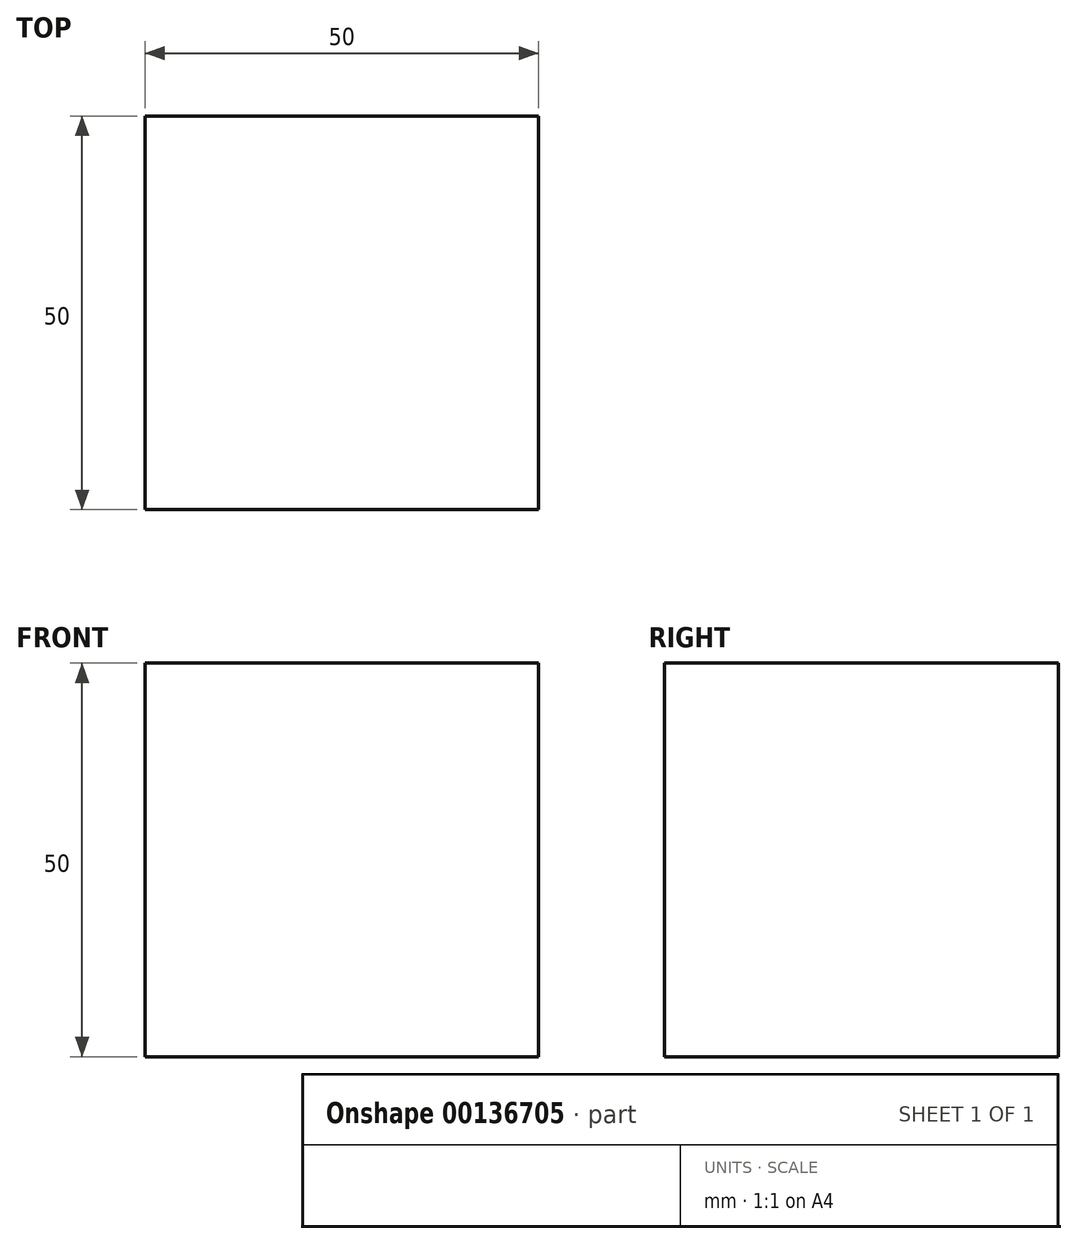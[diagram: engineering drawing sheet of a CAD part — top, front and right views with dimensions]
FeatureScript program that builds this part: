
annotation { "Feature Type Name" : "Feature", "Feature Type Description" : "" }
export const myFeature = defineFeature(function(context is Context, id is Id, definition is map)
    precondition{}
    {
        {
            var Q0;
            Q0=qCreatedBy(makeId("Top.planeOp"),FACE);
            var sketch = newSketch(context, id + "F0", { "sketchPlane" : qUnion([Q0])});
            skLineSegment(sketch, "E0.bottom", {"start": v(-25, -25) * mm, "end": v(25, -25) * mm});
            skLineSegment(sketch, "E0.top", {"start": v(-25, 25) * mm, "end": v(25, 25) * mm});
            skLineSegment(sketch, "E0.left", {"start": v(-25, -25) * mm, "end": v(-25, 25) * mm});
            skLineSegment(sketch, "E0.right", {"start": v(25, -25) * mm, "end": v(25, 25) * mm});
            skPoint(sketch, "E0.middle", {"position": v(0, 0) * mm});
            skSolve(sketch);
        }
        {
            var Q0;
            Q0=makeQuery(id+"F0.imprint","IMPRINT",FACE,{"disambiguationData":[TD([[makeQuery(id+"F0.imprint","IMPRINT",EDGE,{"derivedFrom":sQuery(id+"F0.wireOp",EDGE,"E0.bottom")}),1.0]])]});
            extrude(context, id + "F1", {"entities" : qUnion([Q0]), "depth" : 50 * mm});
        }
    });
